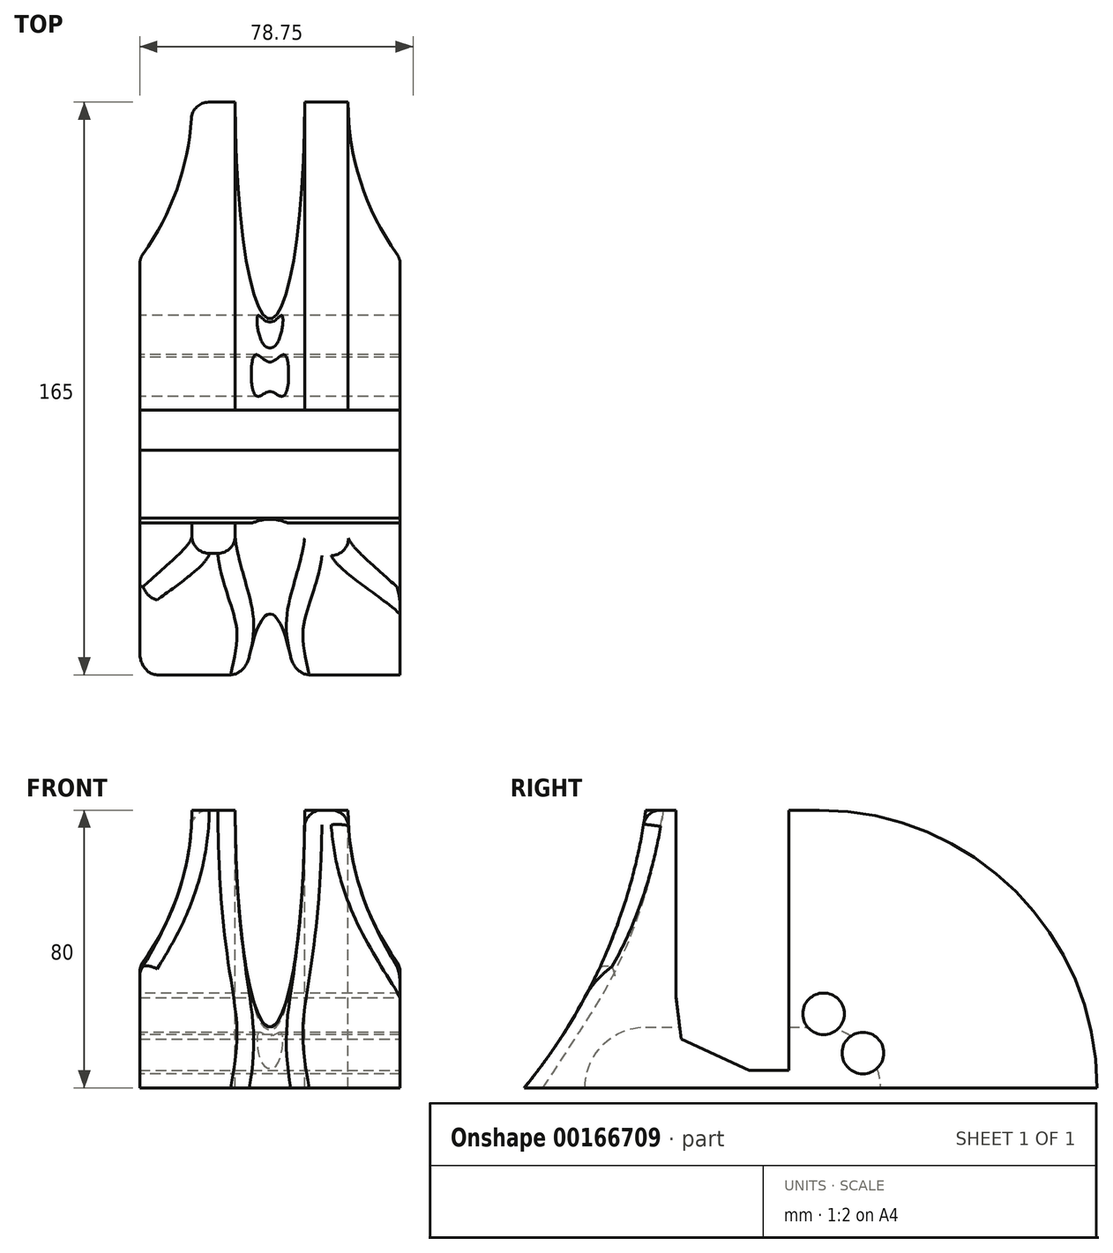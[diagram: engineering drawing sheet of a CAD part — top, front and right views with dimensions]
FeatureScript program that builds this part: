
annotation { "Feature Type Name" : "Feature", "Feature Type Description" : "" }
export const myFeature = defineFeature(function(context is Context, id is Id, definition is map)
    precondition{}
    {
        {
            var Q0;
            Q0=qCreatedBy(makeId("Right.planeOp"),FACE);
            var sketch = newSketch(context, id + "F0", { "sketchPlane" : qUnion([Q0])});
            skLineSegment(sketch, "E0.bottom", {"start": v(-25, 80) * mm, "end": v(25, 80) * mm});
            skLineSegment(sketch, "E0.top", {"start": v(-25, 0) * mm, "end": v(25, 0) * mm});
            skLineSegment(sketch, "E0.left", {"start": v(-25, 80) * mm, "end": v(-25, 0) * mm});
            skLineSegment(sketch, "E0.right", {"start": v(25, 80) * mm, "end": v(25, 0) * mm});
            skSolve(sketch);
        }
        {
            var Q0;
            Q0 = qSketchRegion(id + "F0", true);
            extrude(context, id + "F1", {"entities" : qUnion([Q0]), "endBound" : BoundingType.SYMMETRIC, "depth" : 75 * mm});
        }
        {
            var Q0;
            Q0=makeQuery(id+"F1.opExtrude","CAP_FACE",FACE,{"disambiguationData":[OSD([sQuery(id+"F0.wireOp",EDGE,"E0.bottom"),sQuery(id+"F0.wireOp",EDGE,"E0.top"),sQuery(id+"F0.wireOp",EDGE,"E0.left"),sQuery(id+"F0.wireOp",EDGE,"E0.right")])],"isStart":false});
            var sketch = newSketch(context, id + "F2", { "sketchPlane" : qUnion([Q0])});
            skLineSegment(sketch, "E1", {"start": v(-16.25, 80) * mm, "end": v(-16.25, 26) * mm});
            skLineSegment(sketch, "E2", {"start": v(-16.25, 26) * mm, "end": v(-14.79, 14.09) * mm});
            skLineSegment(sketch, "E3", {"start": v(-14.79, 14.09) * mm, "end": v(4.75, 5) * mm});
            skLineSegment(sketch, "E4", {"start": v(16.25, 5) * mm, "end": v(16.25, 80) * mm});
            skLineSegment(sketch, "E5", {"start": v(4.75, 5) * mm, "end": v(16.25, 5) * mm});
            skLineSegment(sketch, "E6", {"start": v(-16.25, 80) * mm, "end": v(16.25, 80) * mm});
            skSolve(sketch);
        }
        {
            var Q0;
            Q0 = qSketchRegion(id + "F2", true);
            extrude(context, id + "F3", {"entities" : qUnion([Q0]), "operationType" : NewBodyOperationType.REMOVE, "endBound" : BoundingType.UP_TO_NEXT, "oppositeDirection" : true, "depth" : 25 * mm});
        }
        {
            var Q0;
            Q0=makeQuery(id+"F1.opExtrude","SWEPT_FACE",FACE,{"disambiguationData":[OSD([sQuery(id+"F0.wireOp",EDGE,"E0.left")])]});
            var sketch = newSketch(context, id + "F4", { "sketchPlane" : qUnion([Q0])});
            skArc(sketch, "E7", {"start": v(-37.5, 35) * mm, "mid": v(-26.35, 56.28) * mm, "end": v(-22.5, 80) * mm});
            skEllipse(sketch, "E8", {"center": v(0, 80) * mm, "majorRadius": 62.5 * mm, "minorRadius": 10 * mm, "majorAxis": v(0, -1)});
            skPoint(sketch, "E9", {"position": v(10, 80) * mm});
            skLineSegment(sketch, "E10", {"start": v(-37.5, 35) * mm, "end": v(-37.5, 80) * mm});
            skLineSegment(sketch, "E11", {"start": v(-37.5, 80) * mm, "end": v(-22.5, 80) * mm});
            skLineSegment(sketch, "E12.MirrorCS", {"start": v(37.5, 35) * mm, "end": v(37.5, 80) * mm});
            skLineSegment(sketch, "E13.MirrorCS", {"start": v(37.5, 80) * mm, "end": v(22.5, 80) * mm});
            skArc(sketch, "E14.MirrorCS", {"start": v(37.5, 35) * mm, "mid": v(26.35, 56.28) * mm, "end": v(22.5, 80) * mm});
            skSolve(sketch);
        }
        {
            var Q0;
            Q0 = qSketchRegion(id + "F4", true);
            var Q1;
            Q1=makeQuery(id+"F1.opExtrude","SWEPT_FACE",FACE,{"disambiguationData":[OSD([sQuery(id+"F0.wireOp",EDGE,"E0.right")])]});
            extrude(context, id + "F5", {"entities" : qUnion([Q0]), "operationType" : NewBodyOperationType.REMOVE, "endBound" : BoundingType.UP_TO_SURFACE, "oppositeDirection" : true, "endBoundEntityFace" : qUnion([Q1]), "depth" : 25 * mm});
        }
        {
            var Q0;
            Q0=makeQuery(id+"F1.opExtrude","SWEPT_FACE",FACE,{"disambiguationData":[OSD([sQuery(id+"F0.wireOp",EDGE,"E0.right")])]});
            var Q1;
            Q1=makeQuery(id+"F1.opExtrude","SWEPT_EDGE",EDGE,{"disambiguationData":[OSD([sQuery(id+"F0.wireOp",EDGE,"E0.top"),sQuery(id+"F0.wireOp",EDGE,"E0.right")])]});
            revolve(context, id + "F6", {"operationType" : NewBodyOperationType.ADD, "entities" : qUnion([Q0]), "axis" : qUnion([Q1]), "revolveType" : RevolveType.ONE_DIRECTION, "angle" : 90 * degree});
        }
        {
            var Q0;
            Q0=makeQuery(id+"F1.opExtrude","SWEPT_FACE",FACE,{"disambiguationData":[OSD([sQuery(id+"F0.wireOp",EDGE,"E0.left")])]});
            var Q1;
            Q1=makeQuery(id+"F1.opExtrude","SWEPT_EDGE",EDGE,{"disambiguationData":[OSD([sQuery(id+"F0.wireOp",EDGE,"E0.top"),sQuery(id+"F0.wireOp",EDGE,"E0.left")])]});
            revolve(context, id + "F7", {"operationType" : NewBodyOperationType.ADD, "entities" : qUnion([Q0]), "axis" : qUnion([Q1]), "revolveType" : RevolveType.ONE_DIRECTION, "oppositeDirection" : true, "angle" : 90 * degree});
        }
        {
            var Q0;
            {var subQ0=sQuery(id+"F0.wireOp",EDGE,"E0.left");var subQ1=sQuery(id+"F0.wireOp",EDGE,"E0.right");Q0=makeQuery(id+"F7.boolean.opBoolean","MERGE",FACE,{"derivedFrom":[makeQuery(id+"F6.boolean.opBoolean","MERGE",FACE,{"derivedFrom":[makeQuery(id+"F1.opExtrude","CAP_FACE",FACE,{"disambiguationData":[OSD([sQuery(id+"F0.wireOp",EDGE,"E0.bottom"),sQuery(id+"F0.wireOp",EDGE,"E0.top"),subQ0,subQ1])],"isStart":false}),makeQuery(id+"F6.opRevolve","SWEPT_FACE",FACE,{"disambiguationData":[OSD([subQ1]),TDD([makeQuery(id+"F1.opExtrude","CAP_EDGE",EDGE,{"disambiguationData":[OSD([subQ1])],"isStart":false})])]})]}),makeQuery(id+"F7.opRevolve","SWEPT_FACE",FACE,{"disambiguationData":[OSD([subQ0]),TDD([makeQuery(id+"F1.opExtrude","CAP_EDGE",EDGE,{"disambiguationData":[OSD([subQ0])],"isStart":false})])]})]});}
            var sketch = newSketch(context, id + "F8", { "sketchPlane" : qUnion([Q0])});
            skPoint(sketch, "E15.0", {"position": v(-25, 80) * mm});
            skLineSegment(sketch, "E16.0", {"start": v(-60, 0) * mm, "end": v(60, 0) * mm, "construction": true});
            skArc(sketch, "E17", {"start": v(-60, 0) * mm, "mid": v(-36.94, 37.57) * mm, "end": v(-25, 80) * mm});
            skLineSegment(sketch, "E18", {"start": v(-25, 80) * mm, "end": v(-105, 80) * mm});
            skLineSegment(sketch, "E19", {"start": v(-105, 80) * mm, "end": v(-105, 0) * mm});
            skLineSegment(sketch, "E20", {"start": v(-105, 0) * mm, "end": v(-60, 0) * mm});
            skPoint(sketch, "E21.0", {"position": v(-105, 0) * mm});
            skSolve(sketch);
        }
        {
            var Q0;
            Q0 = qSketchRegion(id + "F8", true);
            extrude(context, id + "F9", {"entities" : qUnion([Q0]), "operationType" : NewBodyOperationType.REMOVE, "endBound" : BoundingType.THROUGH_ALL, "oppositeDirection" : true, "depth" : 25 * mm});
        }
        {
            var Q0;
            Q0=makeQuery(id+"F9.boolean.opBoolean","INTERSECT",EDGE,{"disambiguationData":[OD(0.0)],"derivedFrom":[makeQuery(id+"F7.opRevolve","SWEPT_FACE",FACE,{"disambiguationData":[OSD([sQuery(id+"F4.wireOp",EDGE,"E8")])]}),makeQuery(id+"F9.opExtrude","SWEPT_FACE",FACE,{"disambiguationData":[OSD([sQuery(id+"F8.wireOp",EDGE,"E17")])]})]});
            var Q1;
            Q1=makeQuery(id+"F9.boolean.opBoolean","INTERSECT",EDGE,{"disambiguationData":[OD(1.0)],"derivedFrom":[makeQuery(id+"F7.opRevolve","SWEPT_FACE",FACE,{"disambiguationData":[OSD([sQuery(id+"F4.wireOp",EDGE,"E8")])]}),makeQuery(id+"F9.opExtrude","SWEPT_FACE",FACE,{"disambiguationData":[OSD([sQuery(id+"F8.wireOp",EDGE,"E17")])]})]});
            var Q2;
            Q2=makeQuery(id+"F9.boolean.opBoolean","COPY",EDGE,{"derivedFrom":makeQuery(id+"F9.opExtrude","CAP_EDGE",EDGE,{"disambiguationData":[OSD([sQuery(id+"F8.wireOp",EDGE,"E17")])],"isStart":true})});
            var Q3;
            Q3=makeQuery(id+"F9.boolean.opBoolean","INTERSECT",EDGE,{"derivedFrom":[makeQuery(id+"F7.opRevolve","SWEPT_FACE",FACE,{"disambiguationData":[OSD([sQuery(id+"F4.wireOp",EDGE,"E14.MirrorCS")])]}),makeQuery(id+"F9.opExtrude","SWEPT_FACE",FACE,{"disambiguationData":[OSD([sQuery(id+"F8.wireOp",EDGE,"E17")])]})]});
            var Q4;
            Q4=makeQuery(id+"F7.opRevolve","SWEPT_EDGE",EDGE,{"disambiguationData":[OSD([sQuery(id+"F0.wireOp",EDGE,"E0.left"),sQuery(id+"F4.wireOp",EDGE,"E12.MirrorCS"),sQuery(id+"F4.wireOp",EDGE,"E14.MirrorCS")])]});
            var Q5;
            Q5=makeQuery(id+"FsMbj7gjF0hKDwz_1.1.F9.boolean.opBoolean","COPY",EDGE,{"derivedFrom":makeQuery(id+"FsMbj7gjF0hKDwz_1.1.F9.opExtrude","CAP_EDGE",EDGE,{"disambiguationData":[OSD([sQuery(id+"F8.wireOp",EDGE,"E17")])],"isStart":true})});
            var Q6;
            Q6=makeQuery(id+"F6.opRevolve","SWEPT_EDGE",EDGE,{"disambiguationData":[OSD([sQuery(id+"F0.wireOp",EDGE,"E0.left"),sQuery(id+"F0.wireOp",EDGE,"E0.right"),sQuery(id+"F4.wireOp",EDGE,"E12.MirrorCS"),sQuery(id+"F4.wireOp",EDGE,"E14.MirrorCS")])]});
            var Q7;
            Q7=makeQuery(id+"FsMbj7gjF0hKDwz_1.1.F9.boolean.opBoolean","INTERSECT",EDGE,{"derivedFrom":[makeQuery(id+"F6.opRevolve","SWEPT_FACE",FACE,{"disambiguationData":[OSD([sQuery(id+"F0.wireOp",EDGE,"E0.right"),sQuery(id+"F4.wireOp",EDGE,"E14.MirrorCS")])]}),makeQuery(id+"FsMbj7gjF0hKDwz_1.1.F9.opExtrude","SWEPT_FACE",FACE,{"disambiguationData":[OSD([sQuery(id+"F8.wireOp",EDGE,"E17")])]})]});
            var Q8;
            Q8=makeQuery(id+"F6.opRevolve","SWEPT_EDGE",EDGE,{"disambiguationData":[OSD([sQuery(id+"F0.wireOp",EDGE,"E0.left"),sQuery(id+"F0.wireOp",EDGE,"E0.right"),sQuery(id+"F4.wireOp",EDGE,"E7"),sQuery(id+"F4.wireOp",EDGE,"E10")])]});
            var Q9;
            Q9=makeQuery(id+"FsMbj7gjF0hKDwz_1.1.F9.boolean.opBoolean","INTERSECT",EDGE,{"derivedFrom":[makeQuery(id+"F6.opRevolve","SWEPT_FACE",FACE,{"disambiguationData":[OSD([sQuery(id+"F0.wireOp",EDGE,"E0.right"),sQuery(id+"F4.wireOp",EDGE,"E7")])]}),makeQuery(id+"FsMbj7gjF0hKDwz_1.1.F9.opExtrude","SWEPT_FACE",FACE,{"disambiguationData":[OSD([sQuery(id+"F8.wireOp",EDGE,"E17")])]})]});
            var Q10;
            {var subQ0=sQuery(id+"F0.wireOp",EDGE,"E0.left");var subQ1=sQuery(id+"F0.wireOp",EDGE,"E0.right");Q10=makeQuery(id+"F9.boolean.opBoolean","INTERSECT",EDGE,{"derivedFrom":[makeQuery(id+"F7.boolean.opBoolean","MERGE",FACE,{"derivedFrom":[makeQuery(id+"F6.boolean.opBoolean","MERGE",FACE,{"derivedFrom":[makeQuery(id+"F1.opExtrude","CAP_FACE",FACE,{"disambiguationData":[OSD([sQuery(id+"F0.wireOp",EDGE,"E0.bottom"),sQuery(id+"F0.wireOp",EDGE,"E0.top"),subQ0,subQ1])],"isStart":true}),makeQuery(id+"F6.opRevolve","SWEPT_FACE",FACE,{"disambiguationData":[OSD([subQ1]),TDD([makeQuery(id+"F1.opExtrude","CAP_EDGE",EDGE,{"disambiguationData":[OSD([subQ1])],"isStart":true})])]})]}),makeQuery(id+"F7.opRevolve","SWEPT_FACE",FACE,{"disambiguationData":[OSD([subQ0]),TDD([makeQuery(id+"F1.opExtrude","CAP_EDGE",EDGE,{"disambiguationData":[OSD([subQ0])],"isStart":true})])]})]}),makeQuery(id+"F9.opExtrude","SWEPT_FACE",FACE,{"disambiguationData":[OSD([sQuery(id+"F8.wireOp",EDGE,"E17")])]})]});}
            var Q11;
            Q11=makeQuery(id+"F7.opRevolve","SWEPT_EDGE",EDGE,{"disambiguationData":[OSD([sQuery(id+"F0.wireOp",EDGE,"E0.left"),sQuery(id+"F4.wireOp",EDGE,"E7"),sQuery(id+"F4.wireOp",EDGE,"E10")])]});
            var Q12;
            Q12=makeQuery(id+"F9.boolean.opBoolean","INTERSECT",EDGE,{"derivedFrom":[makeQuery(id+"F7.opRevolve","SWEPT_FACE",FACE,{"disambiguationData":[OSD([sQuery(id+"F4.wireOp",EDGE,"E7")])]}),makeQuery(id+"F9.opExtrude","SWEPT_FACE",FACE,{"disambiguationData":[OSD([sQuery(id+"F8.wireOp",EDGE,"E17")])]})]});
            var Q13;
            {var subQ0=sQuery(id+"F0.wireOp",EDGE,"E0.left");var subQ1=sQuery(id+"F0.wireOp",EDGE,"E0.right");Q13=makeQuery(id+"FsMbj7gjF0hKDwz_1.1.F9.boolean.opBoolean","INTERSECT",EDGE,{"derivedFrom":[makeQuery(id+"F7.boolean.opBoolean","MERGE",FACE,{"derivedFrom":[makeQuery(id+"F6.boolean.opBoolean","MERGE",FACE,{"derivedFrom":[makeQuery(id+"F1.opExtrude","CAP_FACE",FACE,{"disambiguationData":[OSD([sQuery(id+"F0.wireOp",EDGE,"E0.bottom"),sQuery(id+"F0.wireOp",EDGE,"E0.top"),subQ0,subQ1])],"isStart":true}),makeQuery(id+"F6.opRevolve","SWEPT_FACE",FACE,{"disambiguationData":[OSD([subQ1]),TDD([makeQuery(id+"F1.opExtrude","CAP_EDGE",EDGE,{"disambiguationData":[OSD([subQ1])],"isStart":true})])]})]}),makeQuery(id+"F7.opRevolve","SWEPT_FACE",FACE,{"disambiguationData":[OSD([subQ0]),TDD([makeQuery(id+"F1.opExtrude","CAP_EDGE",EDGE,{"disambiguationData":[OSD([subQ0])],"isStart":true})])]})]}),makeQuery(id+"FsMbj7gjF0hKDwz_1.1.F9.opExtrude","SWEPT_FACE",FACE,{"disambiguationData":[OSD([sQuery(id+"F8.wireOp",EDGE,"E17")])]})]});}
            fillet(context, id + "F10", {"entities" : qUnion([Q0, Q1, Q2, Q3, Q4, Q5, Q6, Q7, Q8, Q9, Q10, Q11, Q12, Q13]), "radius" : 5 * mm, "tangentPropagation" : true, "allowEdgeOverflow" : false});
        }
        {
            var Q0;
            {var subQ0=sQuery(id+"F0.wireOp",EDGE,"E0.bottom");var subQ1=sQuery(id+"F0.wireOp",EDGE,"E0.left");var subQ2=sQuery(id+"F4.wireOp",EDGE,"E14.MirrorCS");Q0=makeQuery(id+"F5.boolean.opBoolean","COPY",EDGE,{"disambiguationData":[TD([makeQuery(id+"F1.opExtrude","SWEPT_FACE",FACE,{"disambiguationData":[OSD([subQ1])]})])],"derivedFrom":makeQuery(id+"F5.opExtrude","SWEPT_EDGE",EDGE,{"disambiguationData":[OSD([subQ0,subQ1,sQuery(id+"F4.wireOp",EDGE,"E13.MirrorCS"),subQ2])]})});}
            var Q1;
            {var subQ1=sQuery(id+"F0.wireOp",EDGE,"E0.left");var subQ3=sQuery(id+"F0.wireOp",EDGE,"E0.bottom");Q1=makeQuery(id+"F5.boolean.opBoolean","INTERSECT",EDGE,{"disambiguationData":[OD(0.0)],"derivedFrom":[makeQuery(id+"F3.boolean.opBoolean","SPLIT",FACE,{"disambiguationData":[TD([makeQuery(id+"F1.opExtrude","SWEPT_FACE",FACE,{"disambiguationData":[OSD([subQ1])]})])],"derivedFrom":makeQuery(id+"F1.opExtrude","SWEPT_FACE",FACE,{"disambiguationData":[OSD([subQ3])]})}),makeQuery(id+"F5.opExtrude","SWEPT_FACE",FACE,{"disambiguationData":[OSD([sQuery(id+"F4.wireOp",EDGE,"E8")])]})]});}
            var Q2;
            {var subQ0=sQuery(id+"F0.wireOp",EDGE,"E0.bottom");var subQ1=sQuery(id+"F4.wireOp",EDGE,"E7");Q2=makeQuery(id+"F5.boolean.opBoolean","COPY",EDGE,{"disambiguationData":[TD([makeQuery(id+"F1.opExtrude","SWEPT_FACE",FACE,{"disambiguationData":[OSD([sQuery(id+"F0.wireOp",EDGE,"E0.right")])]})])],"derivedFrom":makeQuery(id+"F5.opExtrude","SWEPT_EDGE",EDGE,{"disambiguationData":[OSD([subQ0,sQuery(id+"F0.wireOp",EDGE,"E0.left"),subQ1,sQuery(id+"F4.wireOp",EDGE,"E11")])]})});}
            var Q3;
            {var subQ0=sQuery(id+"F0.wireOp",EDGE,"E0.bottom");var subQ1=sQuery(id+"F4.wireOp",EDGE,"E14.MirrorCS");Q3=makeQuery(id+"F5.boolean.opBoolean","COPY",EDGE,{"disambiguationData":[TD([makeQuery(id+"F1.opExtrude","SWEPT_FACE",FACE,{"disambiguationData":[OSD([sQuery(id+"F0.wireOp",EDGE,"E0.right")])]})])],"derivedFrom":makeQuery(id+"F5.opExtrude","SWEPT_EDGE",EDGE,{"disambiguationData":[OSD([subQ0,sQuery(id+"F0.wireOp",EDGE,"E0.left"),sQuery(id+"F4.wireOp",EDGE,"E13.MirrorCS"),subQ1])]})});}
            fillet(context, id + "F11", {"entities" : qUnion([Q0, Q1, Q2, Q3]), "radius" : 5 * mm, "tangentPropagation" : true, "allowEdgeOverflow" : false});
        }
        {
            var Q0;
            {var subQ0=sQuery(id+"F0.wireOp",EDGE,"E0.left");var subQ1=sQuery(id+"F0.wireOp",EDGE,"E0.right");Q0=makeQuery(id+"F7.boolean.opBoolean","MERGE",FACE,{"derivedFrom":[makeQuery(id+"F6.boolean.opBoolean","MERGE",FACE,{"derivedFrom":[makeQuery(id+"F1.opExtrude","CAP_FACE",FACE,{"disambiguationData":[OSD([sQuery(id+"F0.wireOp",EDGE,"E0.bottom"),sQuery(id+"F0.wireOp",EDGE,"E0.top"),subQ0,subQ1])],"isStart":true}),makeQuery(id+"F6.opRevolve","SWEPT_FACE",FACE,{"disambiguationData":[OSD([subQ1]),TDD([makeQuery(id+"F1.opExtrude","CAP_EDGE",EDGE,{"disambiguationData":[OSD([subQ1])],"isStart":true})])]})]}),makeQuery(id+"F7.opRevolve","SWEPT_FACE",FACE,{"disambiguationData":[OSD([subQ0]),TDD([makeQuery(id+"F1.opExtrude","CAP_EDGE",EDGE,{"disambiguationData":[OSD([subQ0])],"isStart":true})])]})]});}
            var sketch = newSketch(context, id + "F12", { "sketchPlane" : qUnion([Q0])});
            skCircle(sketch, "E22", {"center": v(-37.56, 10) * mm, "radius": 6 * mm});
            skCircle(sketch, "E23", {"center": v(-26.25, 21.31) * mm, "radius": 6 * mm});
            skLineSegment(sketch, "E24", {"start": v(-37.56, 10) * mm, "end": v(-26.25, 21.31) * mm, "construction": true});
            skSolve(sketch);
        }
        {
            var Q0;
            Q0 = qSketchRegion(id + "F12", true);
            extrude(context, id + "F13", {"entities" : qUnion([Q0]), "operationType" : NewBodyOperationType.REMOVE, "endBound" : BoundingType.THROUGH_ALL, "oppositeDirection" : true, "depth" : 25 * mm});
        }
    });
